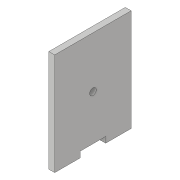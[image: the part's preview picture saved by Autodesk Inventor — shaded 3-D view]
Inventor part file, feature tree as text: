
AUTODESK INVENTOR PART (.ipt)
format: ipt  version: 2017 (Build 210142000, 142)  size: 82,432 bytes
history: native  units: in
note: dims shown in document units (in); Inventor stores cm internally (conversion verified against a paired STEP export)
features: extrude x1, sketch x1
ambient origin geometry x8: Origin, YZ Plane, XZ Plane, XY Plane, X Axis, Y Axis, Z Axis, Center Point
bodies: Solid1 (feature_tree)
feature tree (2):
  extrude  "Extrusion1"  Depth=1.5in
  sketch  "Sketch1"  dims[d0=2.0in d1=1.5in d2=0.13in d3=0.115in d4=0.0in d9=0.5in d10=0.5in d11=0.115in]
